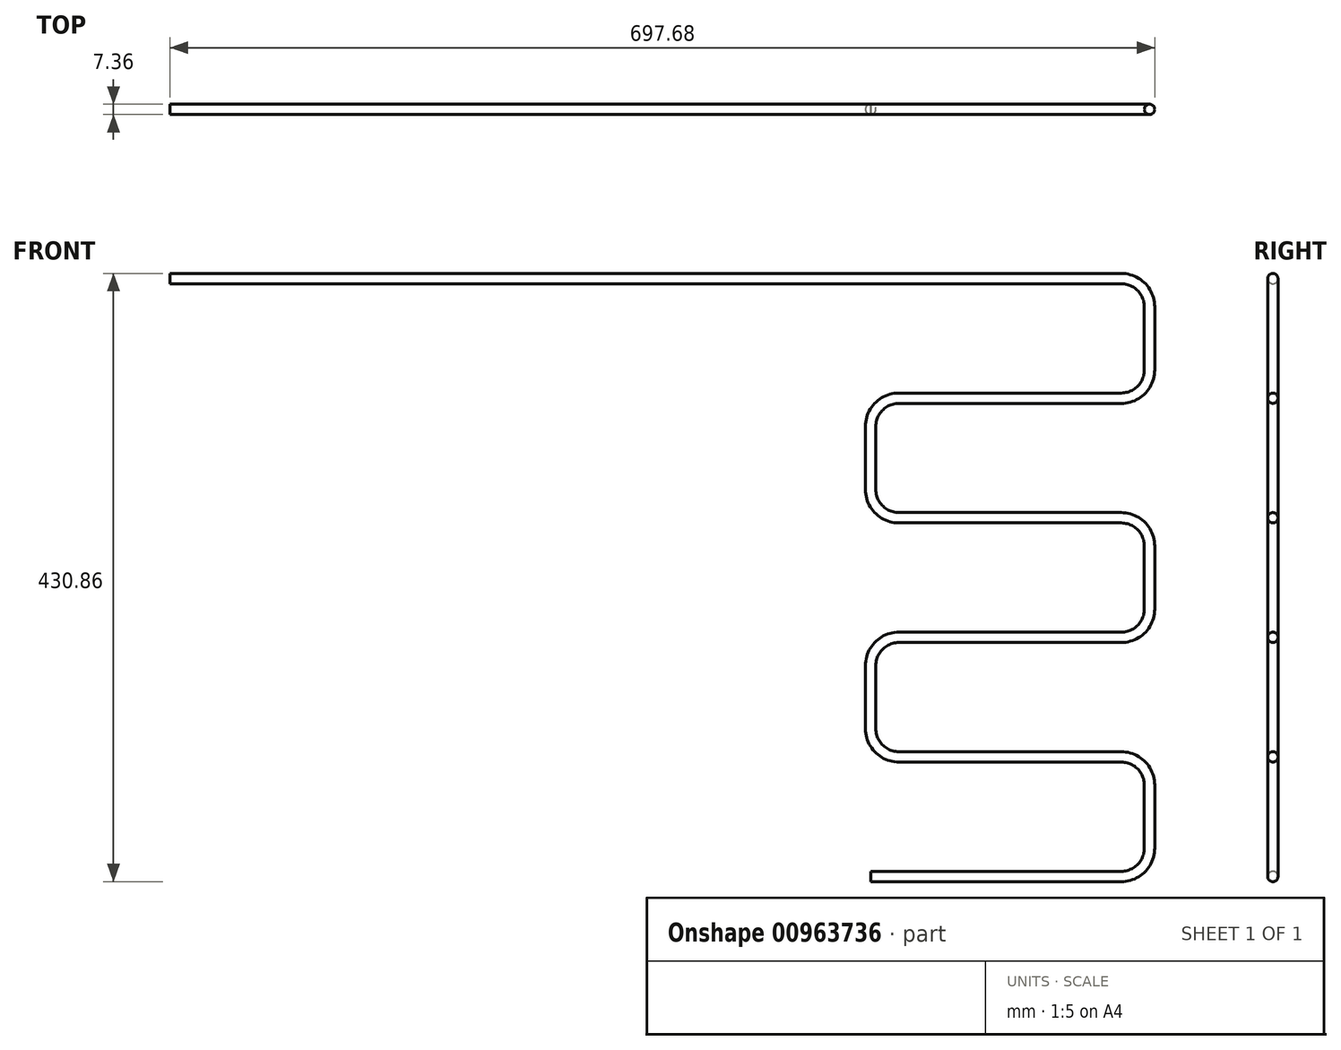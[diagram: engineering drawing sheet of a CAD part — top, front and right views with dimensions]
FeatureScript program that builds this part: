
annotation { "Feature Type Name" : "Feature", "Feature Type Description" : "" }
export const myFeature = defineFeature(function(context is Context, id is Id, definition is map)
    precondition{}
    {
        {
            var Q0;
            Q0=qCreatedBy(makeId("Front.planeOp"),FACE);
            var sketch = newSketch(context, id + "F0", { "sketchPlane" : qUnion([Q0])});
            skLineSegment(sketch, "E0", {"start": v(0, 0) * mm, "end": v(674, 0) * mm});
            skLineSegment(sketch, "E1", {"start": v(694, -20) * mm, "end": v(694, -64.7) * mm});
            skLineSegment(sketch, "E2", {"start": v(674, -84.7) * mm, "end": v(516.4, -84.7) * mm});
            skLineSegment(sketch, "E3", {"start": v(496.4, -104.7) * mm, "end": v(496.4, -149.4) * mm});
            skLineSegment(sketch, "E4", {"start": v(516.4, -169.4) * mm, "end": v(674, -169.4) * mm});
            skLineSegment(sketch, "E5", {"start": v(694, -189.4) * mm, "end": v(694, -234.1) * mm});
            skLineSegment(sketch, "E6", {"start": v(674, -254.1) * mm, "end": v(516.4, -254.1) * mm});
            skLineSegment(sketch, "E7", {"start": v(496.4, -274.1) * mm, "end": v(496.4, -318.8) * mm});
            skLineSegment(sketch, "E8", {"start": v(516.4, -338.8) * mm, "end": v(674, -338.8) * mm});
            skLineSegment(sketch, "E9", {"start": v(694, -358.8) * mm, "end": v(694, -403.5) * mm});
            skLineSegment(sketch, "E10", {"start": v(674, -423.5) * mm, "end": v(496.4, -423.5) * mm});
            skPoint(sketch, "E11.visualSharp", {"position": v(694, 0) * mm});
            skArc(sketch, "E11.filletArc", {"start": v(694, -20) * mm, "mid": v(688.14, -5.86) * mm, "end": v(674, 0) * mm});
            skPoint(sketch, "E12.visualSharp", {"position": v(694, -84.7) * mm});
            skArc(sketch, "E12.filletArc", {"start": v(674, -84.7) * mm, "mid": v(688.14, -78.84) * mm, "end": v(694, -64.7) * mm});
            skPoint(sketch, "E13.visualSharp", {"position": v(496.4, -84.7) * mm});
            skArc(sketch, "E13.filletArc", {"start": v(516.4, -84.7) * mm, "mid": v(502.26, -90.56) * mm, "end": v(496.4, -104.7) * mm});
            skPoint(sketch, "E14.visualSharp", {"position": v(694, -169.4) * mm});
            skArc(sketch, "E14.filletArc", {"start": v(694, -189.4) * mm, "mid": v(688.14, -175.26) * mm, "end": v(674, -169.4) * mm});
            skPoint(sketch, "E15.visualSharp", {"position": v(694, -254.1) * mm});
            skArc(sketch, "E15.filletArc", {"start": v(674, -254.1) * mm, "mid": v(688.14, -248.24) * mm, "end": v(694, -234.1) * mm});
            skPoint(sketch, "E16.visualSharp", {"position": v(496.4, -254.1) * mm});
            skArc(sketch, "E16.filletArc", {"start": v(516.4, -254.1) * mm, "mid": v(502.26, -259.96) * mm, "end": v(496.4, -274.1) * mm});
            skPoint(sketch, "E17.visualSharp", {"position": v(496.4, -338.8) * mm});
            skArc(sketch, "E17.filletArc", {"start": v(496.4, -318.8) * mm, "mid": v(502.26, -332.94) * mm, "end": v(516.4, -338.8) * mm});
            skPoint(sketch, "E18.visualSharp", {"position": v(694, -338.8) * mm});
            skArc(sketch, "E18.filletArc", {"start": v(694, -358.8) * mm, "mid": v(688.14, -344.66) * mm, "end": v(674, -338.8) * mm});
            skPoint(sketch, "E19.visualSharp", {"position": v(496.4, -169.4) * mm});
            skArc(sketch, "E19.filletArc", {"start": v(496.4, -149.4) * mm, "mid": v(502.26, -163.54) * mm, "end": v(516.4, -169.4) * mm});
            skPoint(sketch, "E20.visualSharp", {"position": v(694, -423.5) * mm});
            skArc(sketch, "E20.filletArc", {"start": v(674, -423.5) * mm, "mid": v(688.14, -417.64) * mm, "end": v(694, -403.5) * mm});
            skSolve(sketch);
        }
        {
            var Q0;
            Q0=qCreatedBy(makeId("Right.planeOp"),FACE);
            var sketch = newSketch(context, id + "F1", { "sketchPlane" : qUnion([Q0])});
            skCircle(sketch, "E21", {"center": v(0, 0) * mm, "radius": 3.67 * mm});
            skSolve(sketch);
        }
        {
            var Q0;
            Q0=makeQuery(id+"F1.imprint","IMPRINT",FACE,{"disambiguationData":[TD([[makeQuery(id+"F1.imprint","IMPRINT",EDGE,{"derivedFrom":sQuery(id+"F1.wireOp",EDGE,"E21")}),1.0]])]});
            var Q1;
            Q1=sQuery(id+"F0.wireOp",EDGE,"E0");
            var Q2;
            Q2=sQuery(id+"F0.wireOp",EDGE,"E11.filletArc");
            var Q3;
            Q3=sQuery(id+"F0.wireOp",EDGE,"E1");
            var Q4;
            Q4=sQuery(id+"F0.wireOp",EDGE,"E12.filletArc");
            var Q5;
            Q5=sQuery(id+"F0.wireOp",EDGE,"E2");
            var Q6;
            Q6=sQuery(id+"F0.wireOp",EDGE,"E13.filletArc");
            var Q7;
            Q7=sQuery(id+"F0.wireOp",EDGE,"E3");
            var Q8;
            Q8=sQuery(id+"F0.wireOp",EDGE,"E19.filletArc");
            var Q9;
            Q9=sQuery(id+"F0.wireOp",EDGE,"E4");
            var Q10;
            Q10=sQuery(id+"F0.wireOp",EDGE,"E14.filletArc");
            var Q11;
            Q11=sQuery(id+"F0.wireOp",EDGE,"E5");
            var Q12;
            Q12=sQuery(id+"F0.wireOp",EDGE,"E15.filletArc");
            var Q13;
            Q13=sQuery(id+"F0.wireOp",EDGE,"E6");
            var Q14;
            Q14=sQuery(id+"F0.wireOp",EDGE,"E16.filletArc");
            var Q15;
            Q15=sQuery(id+"F0.wireOp",EDGE,"E7");
            var Q16;
            Q16=sQuery(id+"F0.wireOp",EDGE,"E17.filletArc");
            var Q17;
            Q17=sQuery(id+"F0.wireOp",EDGE,"E8");
            var Q18;
            Q18=sQuery(id+"F0.wireOp",EDGE,"E18.filletArc");
            var Q19;
            Q19=sQuery(id+"F0.wireOp",EDGE,"E9");
            var Q20;
            Q20=sQuery(id+"F0.wireOp",EDGE,"E20.filletArc");
            var Q21;
            Q21=sQuery(id+"F0.wireOp",EDGE,"E10");
            sweep(context, id + "F2", {"profiles" : qUnion([Q0]), "path" : qUnion([Q1, Q2, Q3, Q4, Q5, Q6, Q7, Q8, Q9, Q10, Q11, Q12, Q13, Q14, Q15, Q16, Q17, Q18, Q19, Q20, Q21])});
        }
    });
